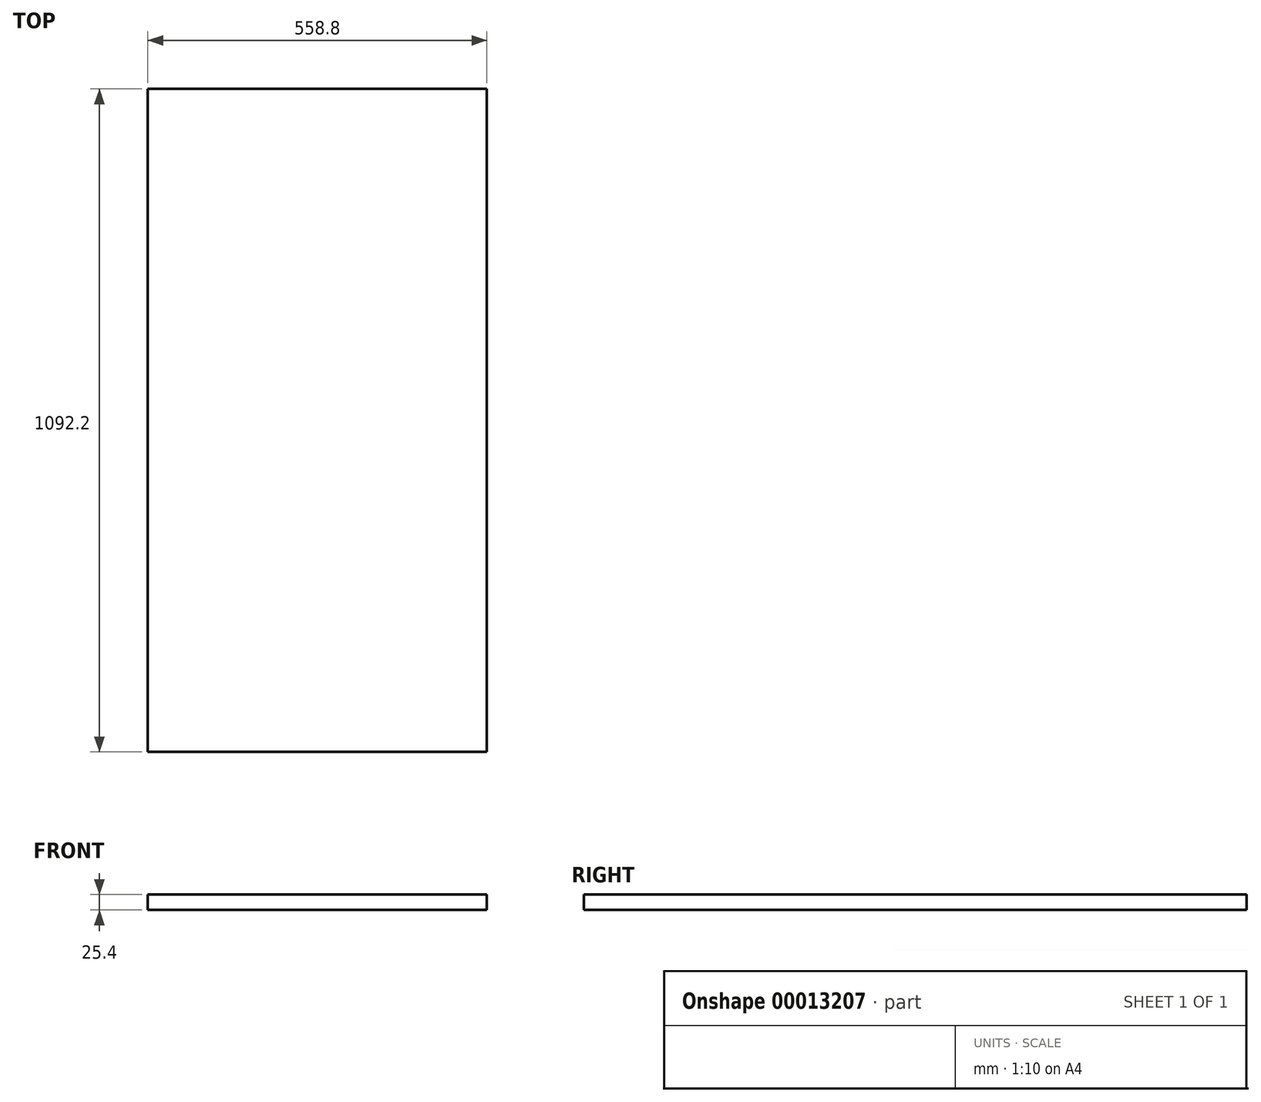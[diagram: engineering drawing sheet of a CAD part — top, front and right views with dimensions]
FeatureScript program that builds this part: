
annotation { "Feature Type Name" : "Feature", "Feature Type Description" : "" }
export const myFeature = defineFeature(function(context is Context, id is Id, definition is map)
    precondition{}
    {
        {
            var Q0;
            Q0=qCreatedBy(makeId("Top.planeOp"),FACE);
            var sketch = newSketch(context, id + "F0", { "sketchPlane" : qUnion([Q0])});
            skLineSegment(sketch, "E0.rect.bottom", {"start": v(279.4, -546.1) * mm, "end": v(-279.4, -546.1) * mm});
            skLineSegment(sketch, "E0.rect.top", {"start": v(279.4, 546.1) * mm, "end": v(-279.4, 546.1) * mm});
            skLineSegment(sketch, "E0.rect.left", {"start": v(279.4, -546.1) * mm, "end": v(279.4, 546.1) * mm});
            skLineSegment(sketch, "E0.rect.right", {"start": v(-279.4, -546.1) * mm, "end": v(-279.4, 546.1) * mm});
            skPoint(sketch, "E0.rect.middle", {"position": v(0, 0) * mm});
            skSolve(sketch);
        }
        {
            var Q0;
            Q0 = qSketchRegion(id + "F0", true);
            extrude(context, id + "F1", {"entities" : qUnion([Q0]), "depth" : 25.4 * mm});
        }
    });
